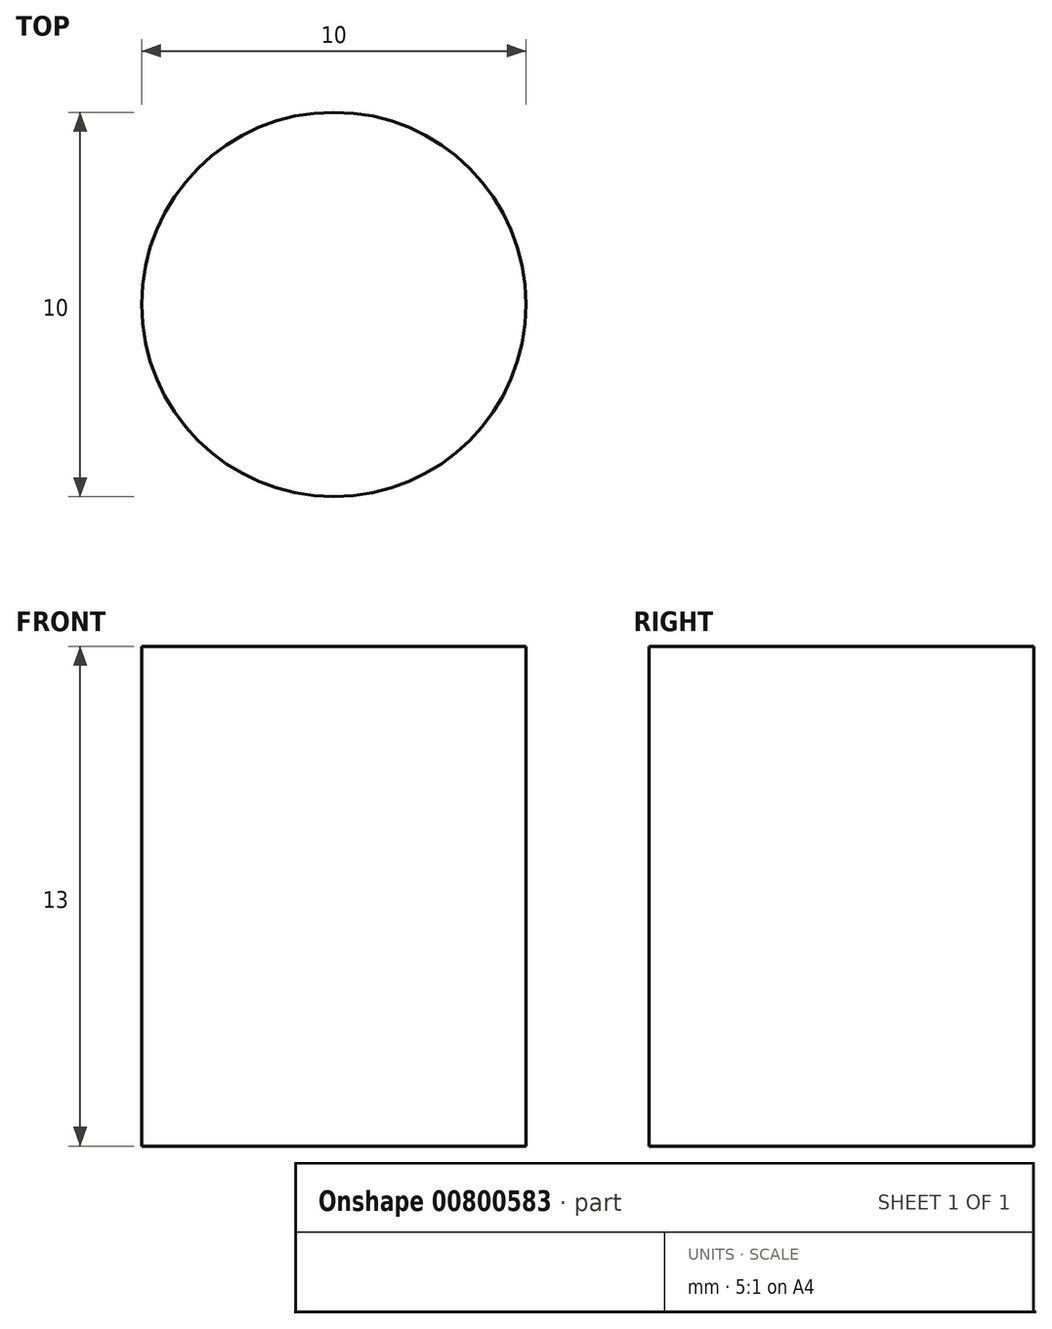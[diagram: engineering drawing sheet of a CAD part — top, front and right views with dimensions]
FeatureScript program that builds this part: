
annotation { "Feature Type Name" : "Feature", "Feature Type Description" : "" }
export const myFeature = defineFeature(function(context is Context, id is Id, definition is map)
    precondition{}
    {
        {
            var Q0;
            Q0=qCreatedBy(makeId("Top.planeOp"),FACE);
            var sketch = newSketch(context, id + "F0", { "sketchPlane" : qUnion([Q0])});
            skCircle(sketch, "E0", {"center": v(0, 0) * mm, "radius": 5 * mm});
            skSolve(sketch);
        }
        {
            var Q0;
            Q0=makeQuery(id+"F0.imprint","IMPRINT",FACE,{"disambiguationData":[TD([[makeQuery(id+"F0.imprint","IMPRINT",EDGE,{"derivedFrom":sQuery(id+"F0.wireOp",EDGE,"E0")}),1.0]])]});
            extrude(context, id + "F1", {"entities" : qUnion([Q0]), "depth" : 13 * mm, "offsetDistance" : 25.4 * mm});
        }
    });
